# Revit family: Konsole 35- 42 Platte längs
name_source: partatom
category: HLS-Bauteile
revit_build: Autodesk Revit 2017 (Build: 20190507_1515(x64)
units: mm (PartAtom-declared; Revit-internal decimal feet)

## family parameters
Basisbauteil = Fläche
Beim Laden mit Abzugskörper schneiden = Nein
Bemaßung runder Anschluss = Durchmesser verwenden
Gemeinsam genutzt = Ja
Raumberechnungspunkt = Nein
Teiletyp = Normal

## types (5) — shared parameters
Ausrichtung Platte = längs
Breite Platte = 40 mm  [stored 0.131234 ft]
Breite Profil = 35 mm  [stored 0.114829 ft]
Fabrikat = MEFA
Firma = MEFA Befestigungs- und Montagesysteme GmbH
Höhe Profil = 42 mm  [stored 0.137795 ft]
Kurztext1 = Konsole Stex 35/42
Langloch Platte = 11x15 mm
Lochabstand = 80 mm
Lochdurchmesser = 11 mm
Länge Platte = 111 mm
Material = Stahl
Materialname C-Profil = S235JR
Materialname Platte = S235JR
Oberflaeche = galvanisch verzinkt
Profil = Stex
Stärke Platte = 8 mm  [stored 0.0262467 ft]
Stärke Profil = 2 mm  [stored 0.00656168 ft]
Vorgabe-Ansicht = 1219 mm

## per-type parameters (varying)
| type | Artikelnummer | EAN | Gewicht | Gewicht pro Bauteil | Kurztext2 | Länge Konsole | Schienenlänge | max. zul. Last F1 | max. zul. Last F2 | max. zul. Last q0 |
| Konsole 35- 42 L=  600 Platte längs gvz | 12760600 | 4250928424594 | 1.24 kg | 1.24 kg | L= 600 mm Platte längs gvz | 600 mm | Montageschiene 35- 42-1,5 für Konsole : C-Profil 35- 42-1,5 L=  600 | 0.23 kip | 0.11 kip | 0.119 kip/ft |
| Konsole 35- 42 L=  525 Platte längs gvz | 12760525 | 4250928424587 | 1.12 kg | 1.12 kg | L= 525 mm Platte längs gvz | 525 mm | Montageschiene 35- 42-1,5 für Konsole : C-Profil 35- 42-1,5 L=  525 | 0.27 kip | 0.13 kip | 0.156 kip/ft |
| Konsole 35- 42 L=  450 Platte längs gvz | 12760450 | 4250928424563 | 1.00 kg | 1.00 kg | L= 450 mm Platte längs gvz | 450 mm  [stored 1.47638 ft] | Montageschiene 35- 42-1,5 für Konsole : C-Profil 35- 42-1,5 L=  450 | 0.31 kip | 0.16 kip | 0.212 kip/ft |
| Konsole 35- 42 L=  300 Platte längs gvz | 12760300 | 4250928424549 | 0.75 kg | 0.75 kg | L= 300 mm Platte längs gvz | 300 mm | Montageschiene 35- 42-1,5 für Konsole : C-Profil 35- 42-1,5 L=  300 | 0.47 kip | 0.23 kip | 0.476 kip/ft |
| Konsole 35- 42 L=  225 Platte längs gvz | 12760225 | 4250928424532 | 0.63 kg | 0.63 kg | L= 225 mm Platte längs gvz | 225 mm  [stored 0.738189 ft] | Montageschiene 35- 42-1,5 für Konsole : C-Profil 35- 42-1,5 L=  225 | 0.62 kip | 0.31 kip | 0.846 kip/ft |

note: [stored X ft] marks values corroborated as IEEE doubles in the binary element streams (Revit-internal decimal feet)
